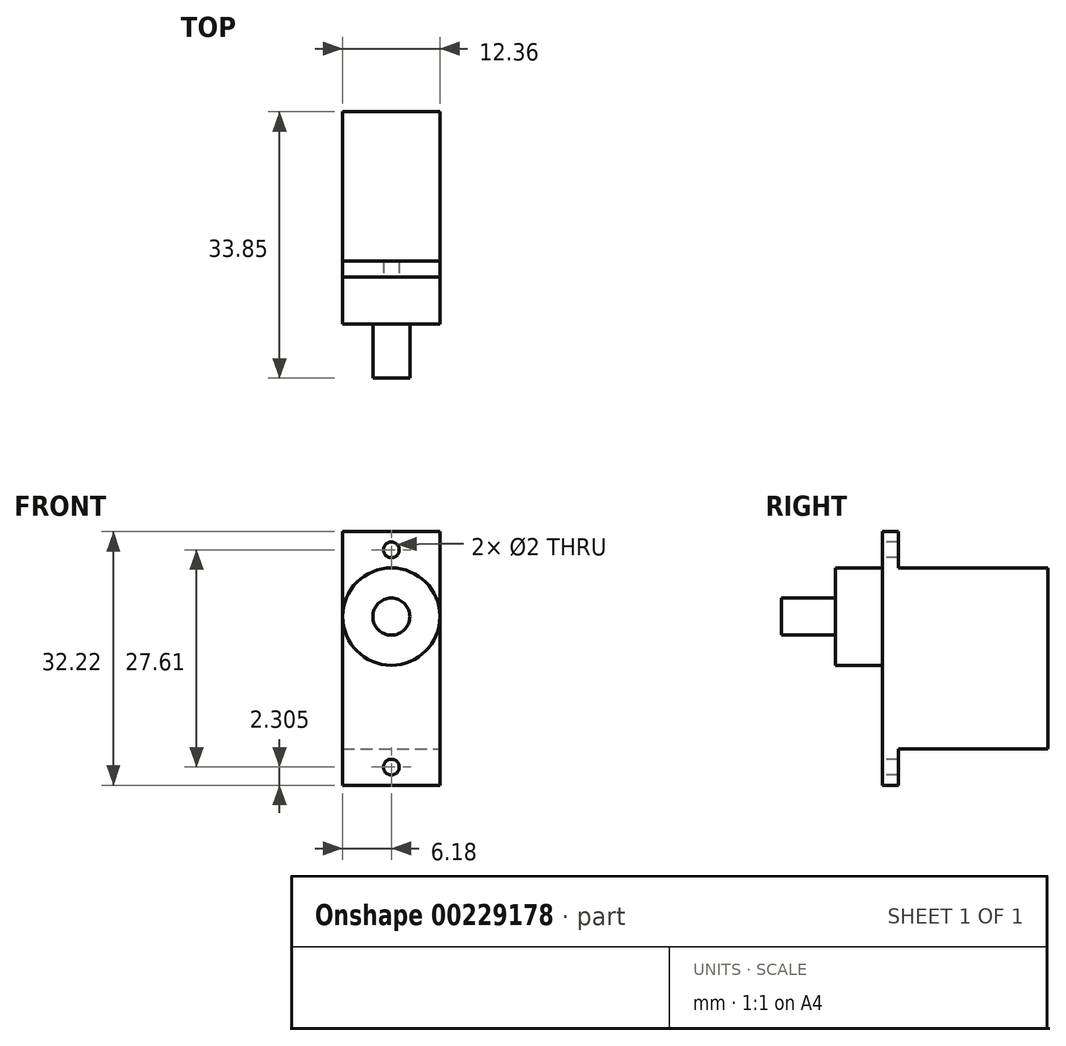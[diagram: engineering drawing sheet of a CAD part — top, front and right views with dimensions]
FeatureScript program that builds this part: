
annotation { "Feature Type Name" : "Feature", "Feature Type Description" : "" }
export const myFeature = defineFeature(function(context is Context, id is Id, definition is map)
    precondition{}
    {
        {
            var Q0;
            Q0=qCreatedBy(makeId("Front.planeOp"),FACE);
            var sketch = newSketch(context, id + "F0", { "sketchPlane" : qUnion([Q0])});
            skLineSegment(sketch, "E0.bottom", {"start": v(-6.18, 16.1) * mm, "end": v(6.18, 16.1) * mm});
            skLineSegment(sketch, "E0.top", {"start": v(-6.18, -16.1) * mm, "end": v(6.18, -16.1) * mm});
            skLineSegment(sketch, "E0.left", {"start": v(-6.18, 16.1) * mm, "end": v(-6.18, -16.1) * mm});
            skLineSegment(sketch, "E0.right", {"start": v(6.18, 16.1) * mm, "end": v(6.18, -16.1) * mm});
            skPoint(sketch, "E0.middle", {"position": v(0, 0) * mm});
            skLineSegment(sketch, "E1", {"start": v(-6.18, 11.5) * mm, "end": v(6.18, 11.5) * mm});
            skLineSegment(sketch, "E2", {"start": v(-6.18, -11.5) * mm, "end": v(6.18, -11.5) * mm});
            skCircle(sketch, "E3", {"center": v(0, 5.32) * mm, "radius": 6.18 * mm});
            skLineSegment(sketch, "E4", {"start": v(-6.18, 16.1) * mm, "end": v(6.18, 11.5) * mm, "construction": true});
            skLineSegment(sketch, "E5", {"start": v(6.18, 16.11) * mm, "end": v(-6.18, 11.5) * mm, "construction": true});
            skLineSegment(sketch, "E6", {"start": v(-6.18, -11.5) * mm, "end": v(6.18, -16.1) * mm, "construction": true});
            skLineSegment(sketch, "E7", {"start": v(6.18, -11.5) * mm, "end": v(-6.18, -16.11) * mm, "construction": true});
            skCircle(sketch, "E8", {"center": v(0, 13.8) * mm, "radius": 1 * mm});
            skCircle(sketch, "E9", {"center": v(0, -13.8) * mm, "radius": 1 * mm});
            skLineSegment(sketch, "E10", {"start": v(0, -11.5) * mm, "end": v(0, -16.1) * mm, "construction": true});
            skLineSegment(sketch, "E11", {"start": v(6.18, -13.8) * mm, "end": v(-5.73, -13.8) * mm, "construction": true});
            skLineSegment(sketch, "E12", {"start": v(-6.18, 13.8) * mm, "end": v(5.4, 13.8) * mm, "construction": true});
            skLineSegment(sketch, "E13", {"start": v(0, 16.1) * mm, "end": v(0, 11.5) * mm, "construction": true});
            skSolve(sketch);
        }
        {
            var Q0;
            {var subQ0=sQuery(id+"F0.wireOp",EDGE,"E1");var subQ1=sQuery(id+"F0.wireOp",EDGE,"E0.left");var subQ2=makeQuery(id+"F0.imprint","INTERSECT",VERTEX,{"derivedFrom":[subQ1,subQ0]});Q0=makeQuery(id+"F0.imprint","IMPRINT",FACE,{"disambiguationData":[TD([[makeQuery(id+"F0.imprint","IMPRINT",EDGE,{"disambiguationData":[TD([[subQ2,-1.0]])],"derivedFrom":subQ1}),1.0]])]});}
            var Q1;
            {var subQ0=sQuery(id+"F0.wireOp",EDGE,"E2");Q1=makeQuery(id+"F0.imprint","IMPRINT",FACE,{"disambiguationData":[TD([[makeQuery(id+"F0.imprint","IMPRINT",EDGE,{"derivedFrom":subQ0}),1.0]])]});}
            var Q2;
            {var subQ0=sQuery(id+"F0.wireOp",EDGE,"E1");var subQ1=sQuery(id+"F0.wireOp",EDGE,"E0.right");var subQ2=makeQuery(id+"F0.imprint","INTERSECT",VERTEX,{"derivedFrom":[subQ1,subQ0]});Q2=makeQuery(id+"F0.imprint","IMPRINT",FACE,{"disambiguationData":[TD([[makeQuery(id+"F0.imprint","IMPRINT",EDGE,{"disambiguationData":[TD([[subQ2,-1.0]])],"derivedFrom":subQ1}),-1.0]])]});}
            var Q3;
            {var subQ0=sQuery(id+"F0.wireOp",EDGE,"E3");var subQ1=makeQuery(id+"F0.imprint","INTERSECT",VERTEX,{"derivedFrom":[sQuery(id+"F0.wireOp",EDGE,"E0.right"),subQ0]});Q3=makeQuery(id+"F0.imprint","IMPRINT",FACE,{"disambiguationData":[TD([[makeQuery(id+"F0.imprint","IMPRINT",EDGE,{"disambiguationData":[TD([[subQ1,-1.0]])],"derivedFrom":subQ0}),1.0]])]});}
            extrude(context, id + "F1", {"entities" : qUnion([Q0, Q1, Q2, Q3]), "oppositeDirection" : true, "depth" : 21 * mm});
        }
        {
            var Q0;
            {var subQ1=sQuery(id+"F0.wireOp",EDGE,"E0.bottom");Q0=makeQuery(id+"F0.imprint","IMPRINT",FACE,{"disambiguationData":[TD([[makeQuery(id+"F0.imprint","IMPRINT",EDGE,{"derivedFrom":subQ1}),-1.0]])]});}
            var Q1;
            {var subQ0=sQuery(id+"F0.wireOp",EDGE,"E0.top");Q1=makeQuery(id+"F0.imprint","IMPRINT",FACE,{"disambiguationData":[TD([[makeQuery(id+"F0.imprint","IMPRINT",EDGE,{"derivedFrom":subQ0}),1.0]])]});}
            extrude(context, id + "F2", {"entities" : qUnion([Q0, Q1]), "operationType" : NewBodyOperationType.ADD, "oppositeDirection" : true, "depth" : 2 * mm});
        }
        {
            var Q0;
            {var subQ0=sQuery(id+"F0.wireOp",EDGE,"E3");var subQ1=makeQuery(id+"F0.imprint","INTERSECT",VERTEX,{"derivedFrom":[sQuery(id+"F0.wireOp",EDGE,"E0.right"),subQ0]});Q0=makeQuery(id+"F0.imprint","IMPRINT",FACE,{"disambiguationData":[TD([[makeQuery(id+"F0.imprint","IMPRINT",EDGE,{"disambiguationData":[TD([[subQ1,-1.0]])],"derivedFrom":subQ0}),1.0]])]});}
            extrude(context, id + "F3", {"entities" : qUnion([Q0]), "operationType" : NewBodyOperationType.ADD, "depth" : 6 * mm});
        }
        {
            var Q0;
            Q0=makeQuery(id+"F3.opExtrude","CAP_FACE",FACE,{"disambiguationData":[OSD([sQuery(id+"F0.wireOp",EDGE,"E3")])],"isStart":false});
            var sketch = newSketch(context, id + "F4", { "sketchPlane" : qUnion([Q0])});
            skCircle(sketch, "E14", {"center": v(0, 5.32) * mm, "radius": 2.35 * mm});
            skSolve(sketch);
        }
        {
            var Q0;
            Q0=makeQuery(id+"F4.imprint","IMPRINT",FACE,{"disambiguationData":[TD([[makeQuery(id+"F4.imprint","IMPRINT",EDGE,{"derivedFrom":sQuery(id+"F4.wireOp",EDGE,"E14")}),1.0]])]});
            extrude(context, id + "F5", {"entities" : qUnion([Q0]), "operationType" : NewBodyOperationType.ADD, "depth" : 12.85 * mm - 6 * mm});
        }
    });
